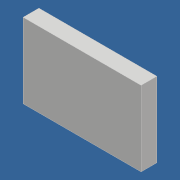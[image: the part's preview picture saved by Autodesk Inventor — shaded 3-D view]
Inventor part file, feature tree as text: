
AUTODESK INVENTOR PART (.ipt)
format: ipt  version: 2017 (Build 210142000, 142)  size: 84,480 bytes
history: native  units: mm
features: extrude x2, sketch x2
ambient origin geometry x8: Origin, YZ Plane, XZ Plane, XY Plane, X Axis, Y Axis, Z Axis, Center Point
bodies: Solid1 (feature_tree)
feature tree (4):
  extrude  "Extrusion1"  Depth=33.02mm
  extrude  "Extrusion2"  Depth=4.0mm
  sketch  "Sketch1"  dims[d0=52.07mm d1=33.02mm]
  sketch  "Sketch2"  dims[d2=7.0mm d3=0.0mm d4=4.0mm d5=4.0mm d6=0.0mm]
